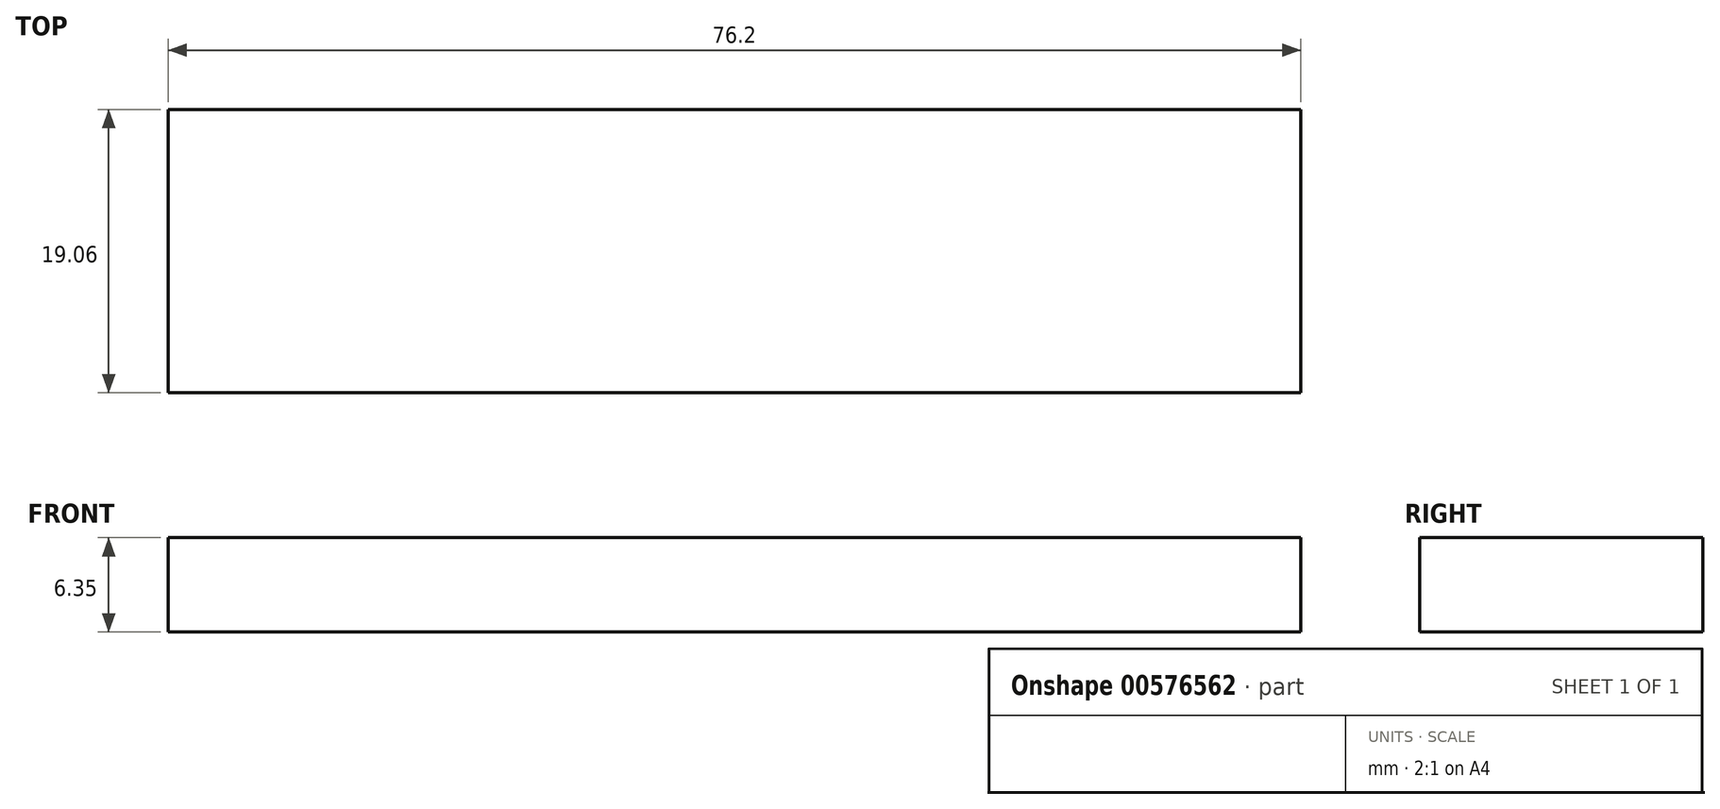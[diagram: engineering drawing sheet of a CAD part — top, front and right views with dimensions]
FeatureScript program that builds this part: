
annotation { "Feature Type Name" : "Feature", "Feature Type Description" : "" }
export const myFeature = defineFeature(function(context is Context, id is Id, definition is map)
    precondition{}
    {
        {
            var Q0;
            Q0=qCreatedBy(makeId("Top.planeOp"),FACE);
            var sketch = newSketch(context, id + "F0", { "sketchPlane" : qUnion([Q0])});
            skLineSegment(sketch, "E0.bottom", {"start": v(-38.1, 9.53) * mm, "end": v(38.1, 9.53) * mm});
            skLineSegment(sketch, "E0.top", {"start": v(-38.1, -9.53) * mm, "end": v(38.1, -9.53) * mm});
            skLineSegment(sketch, "E0.left", {"start": v(-38.1, 9.53) * mm, "end": v(-38.1, -9.53) * mm});
            skLineSegment(sketch, "E0.right", {"start": v(38.1, 9.53) * mm, "end": v(38.1, -9.53) * mm});
            skPoint(sketch, "E0.middle", {"position": v(0, 0) * mm});
            skSolve(sketch);
        }
        {
            var Q0;
            Q0=makeQuery(id+"F0.imprint","IMPRINT",FACE,{"disambiguationData":[TD([[makeQuery(id+"F0.imprint","IMPRINT",EDGE,{"derivedFrom":sQuery(id+"F0.wireOp",EDGE,"E0.bottom")}),-1.0]])]});
            extrude(context, id + "F1", {"entities" : qUnion([Q0]), "depth" : 6.35 * mm, "offsetDistance" : 25.4 * mm});
        }
    });
